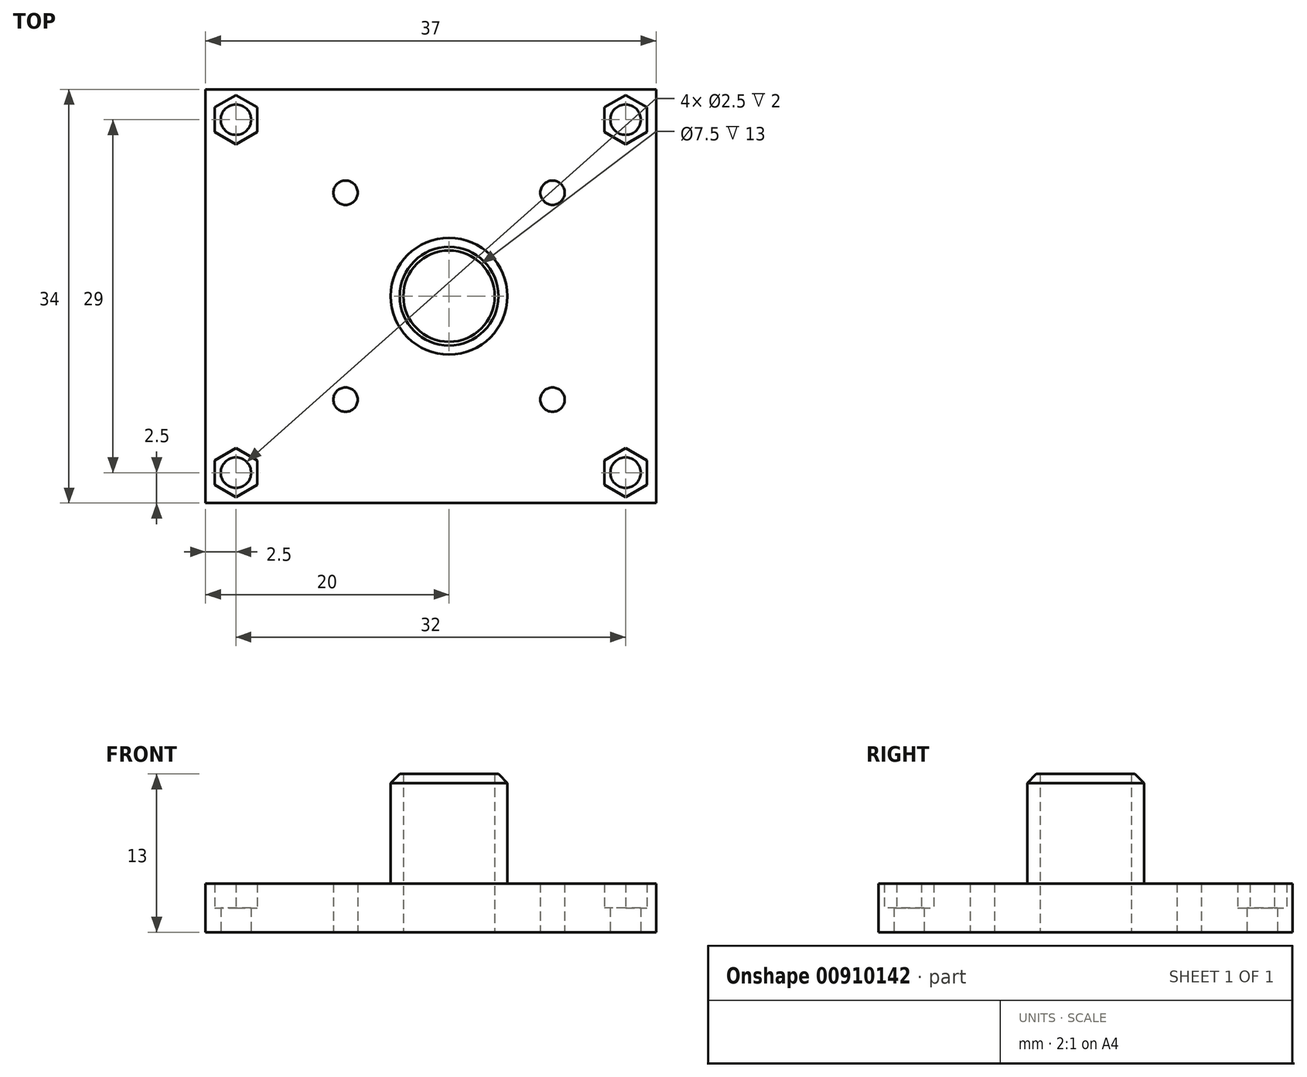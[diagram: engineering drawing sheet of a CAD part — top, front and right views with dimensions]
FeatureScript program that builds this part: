
annotation { "Feature Type Name" : "Feature", "Feature Type Description" : "" }
export const myFeature = defineFeature(function(context is Context, id is Id, definition is map)
    precondition{}
    {
        {
            var Q0;
            Q0=qCreatedBy(makeId("Top.planeOp"),FACE);
            var sketch = newSketch(context, id + "F0", { "sketchPlane" : qUnion([Q0])});
            skCircle(sketch, "E0", {"center": v(0, 0) * mm, "radius": 3.75 * mm});
            skCircle(sketch, "E1", {"center": v(0, 0) * mm, "radius": 4.8 * mm});
            skLineSegment(sketch, "E2.bottom", {"start": v(-20, 17) * mm, "end": v(17, 17) * mm});
            skLineSegment(sketch, "E2.top", {"start": v(-20, -17) * mm, "end": v(17, -17) * mm});
            skLineSegment(sketch, "E2.left", {"start": v(-20, 17) * mm, "end": v(-20, -17) * mm});
            skLineSegment(sketch, "E2.right", {"start": v(17, 17) * mm, "end": v(17, -17) * mm});
            skCircle(sketch, "E3", {"center": v(-17.5, 14.5) * mm, "radius": 1.25 * mm});
            skCircle(sketch, "E4", {"center": v(14.5, 14.5) * mm, "radius": 1.25 * mm});
            skCircle(sketch, "E5", {"center": v(-17.5, -14.5) * mm, "radius": 1.25 * mm});
            skCircle(sketch, "E6", {"center": v(14.5, -14.5) * mm, "radius": 1.25 * mm});
            skCircle(sketch, "E7", {"center": v(8.5, 8.5) * mm, "radius": 1 * mm});
            skCircle(sketch, "E8", {"center": v(8.5, -8.5) * mm, "radius": 1 * mm});
            skCircle(sketch, "E9", {"center": v(-8.5, 8.5) * mm, "radius": 1 * mm});
            skCircle(sketch, "E10", {"center": v(-8.5, -8.5) * mm, "radius": 1 * mm});
            skCircle(sketch, "E11.cCircle", {"center": v(-17.5, 14.5) * mm, "radius": 1.75 * mm, "construction": true});
            skLineSegment(sketch, "E11.0", {"start": v(-17.5, 16.52) * mm, "end": v(-15.75, 15.51) * mm});
            skLineSegment(sketch, "E11.1", {"start": v(-15.75, 15.51) * mm, "end": v(-15.75, 13.49) * mm});
            skLineSegment(sketch, "E11.2", {"start": v(-15.75, 13.49) * mm, "end": v(-17.5, 12.48) * mm});
            skLineSegment(sketch, "E11.3", {"start": v(-17.5, 12.48) * mm, "end": v(-19.25, 13.49) * mm});
            skLineSegment(sketch, "E11.4", {"start": v(-19.25, 13.49) * mm, "end": v(-19.25, 15.51) * mm});
            skLineSegment(sketch, "E11.5", {"start": v(-19.25, 15.51) * mm, "end": v(-17.5, 16.52) * mm});
            skPoint(sketch, "E11.0.midPoint", {"position": v(-16.62, 16.02) * mm});
            skCircle(sketch, "E12.cCircle", {"center": v(14.5, 14.5) * mm, "radius": 1.75 * mm, "construction": true});
            skLineSegment(sketch, "E12.0", {"start": v(12.75, 13.49) * mm, "end": v(12.75, 15.51) * mm});
            skLineSegment(sketch, "E12.1", {"start": v(12.75, 15.51) * mm, "end": v(14.5, 16.52) * mm});
            skLineSegment(sketch, "E12.2", {"start": v(14.5, 16.52) * mm, "end": v(16.25, 15.51) * mm});
            skLineSegment(sketch, "E12.3", {"start": v(16.25, 15.51) * mm, "end": v(16.25, 13.49) * mm});
            skLineSegment(sketch, "E12.4", {"start": v(16.25, 13.49) * mm, "end": v(14.5, 12.48) * mm});
            skLineSegment(sketch, "E12.5", {"start": v(14.5, 12.48) * mm, "end": v(12.75, 13.49) * mm});
            skPoint(sketch, "E12.0.midPoint", {"position": v(12.75, 14.5) * mm});
            skCircle(sketch, "E13.cCircle", {"center": v(14.5, -14.5) * mm, "radius": 1.75 * mm, "construction": true});
            skLineSegment(sketch, "E13.0", {"start": v(12.75, -15.51) * mm, "end": v(12.75, -13.49) * mm});
            skLineSegment(sketch, "E13.1", {"start": v(12.75, -13.49) * mm, "end": v(14.5, -12.48) * mm});
            skLineSegment(sketch, "E13.2", {"start": v(14.5, -12.48) * mm, "end": v(16.25, -13.49) * mm});
            skLineSegment(sketch, "E13.3", {"start": v(16.25, -13.49) * mm, "end": v(16.25, -15.51) * mm});
            skLineSegment(sketch, "E13.4", {"start": v(16.25, -15.51) * mm, "end": v(14.5, -16.52) * mm});
            skLineSegment(sketch, "E13.5", {"start": v(14.5, -16.52) * mm, "end": v(12.75, -15.51) * mm});
            skPoint(sketch, "E13.0.midPoint", {"position": v(12.75, -14.5) * mm});
            skCircle(sketch, "E14.cCircle", {"center": v(-17.5, -14.5) * mm, "radius": 1.75 * mm, "construction": true});
            skLineSegment(sketch, "E14.0", {"start": v(-19.25, -13.49) * mm, "end": v(-17.5, -12.48) * mm});
            skLineSegment(sketch, "E14.1", {"start": v(-17.5, -12.48) * mm, "end": v(-15.75, -13.49) * mm});
            skLineSegment(sketch, "E14.2", {"start": v(-15.75, -13.49) * mm, "end": v(-15.75, -15.51) * mm});
            skLineSegment(sketch, "E14.3", {"start": v(-15.75, -15.51) * mm, "end": v(-17.5, -16.52) * mm});
            skLineSegment(sketch, "E14.4", {"start": v(-17.5, -16.52) * mm, "end": v(-19.25, -15.51) * mm});
            skLineSegment(sketch, "E14.5", {"start": v(-19.25, -15.51) * mm, "end": v(-19.25, -13.49) * mm});
            skPoint(sketch, "E14.0.midPoint", {"position": v(-18.38, -12.98) * mm});
            skSolve(sketch);
        }
        {
            var Q0;
            Q0=makeQuery(id+"F0.imprint","IMPRINT",FACE,{"disambiguationData":[TD([[makeQuery(id+"F0.imprint","IMPRINT",EDGE,{"derivedFrom":sQuery(id+"F0.wireOp",EDGE,"E1")}),-1.0]])]});
            extrude(context, id + "F1", {"entities" : qUnion([Q0]), "depth" : 4 * mm, "offsetDistance" : 25 * mm});
        }
        {
            var Q0;
            Q0=makeQuery(id+"F0.imprint","IMPRINT",FACE,{"disambiguationData":[TD([[makeQuery(id+"F0.imprint","IMPRINT",EDGE,{"derivedFrom":sQuery(id+"F0.wireOp",EDGE,"E0")}),-1.0]])]});
            extrude(context, id + "F2", {"entities" : qUnion([Q0]), "operationType" : NewBodyOperationType.ADD, "depth" : 13 * mm, "offsetDistance" : 25 * mm});
        }
        {
            var Q0;
            Q0=makeQuery(id+"F2.opExtrude","CAP_EDGE",EDGE,{"disambiguationData":[OSD([sQuery(id+"F0.wireOp",EDGE,"E1")])],"isStart":false});
            chamfer(context, id + "F3", {"entities" : qUnion([Q0]), "width" : 0.75 * mm, "tangentPropagation" : true});
        }
        {
            var Q0;
            Q0=makeQuery(id+"F0.imprint","IMPRINT",FACE,{"disambiguationData":[TD([[makeQuery(id+"F0.imprint","IMPRINT",EDGE,{"derivedFrom":sQuery(id+"F0.wireOp",EDGE,"E5")}),-1.0]])]});
            var Q1;
            Q1=makeQuery(id+"F0.imprint","IMPRINT",FACE,{"disambiguationData":[TD([[makeQuery(id+"F0.imprint","IMPRINT",EDGE,{"derivedFrom":sQuery(id+"F0.wireOp",EDGE,"E6")}),-1.0]])]});
            var Q2;
            Q2=makeQuery(id+"F0.imprint","IMPRINT",FACE,{"disambiguationData":[TD([[makeQuery(id+"F0.imprint","IMPRINT",EDGE,{"derivedFrom":sQuery(id+"F0.wireOp",EDGE,"E4")}),-1.0]])]});
            var Q3;
            Q3=makeQuery(id+"F0.imprint","IMPRINT",FACE,{"disambiguationData":[TD([[makeQuery(id+"F0.imprint","IMPRINT",EDGE,{"derivedFrom":sQuery(id+"F0.wireOp",EDGE,"E3")}),-1.0]])]});
            extrude(context, id + "F4", {"entities" : qUnion([Q0, Q1, Q2, Q3]), "operationType" : NewBodyOperationType.ADD, "depth" : 2 * mm, "offsetDistance" : 25 * mm});
        }
    });
